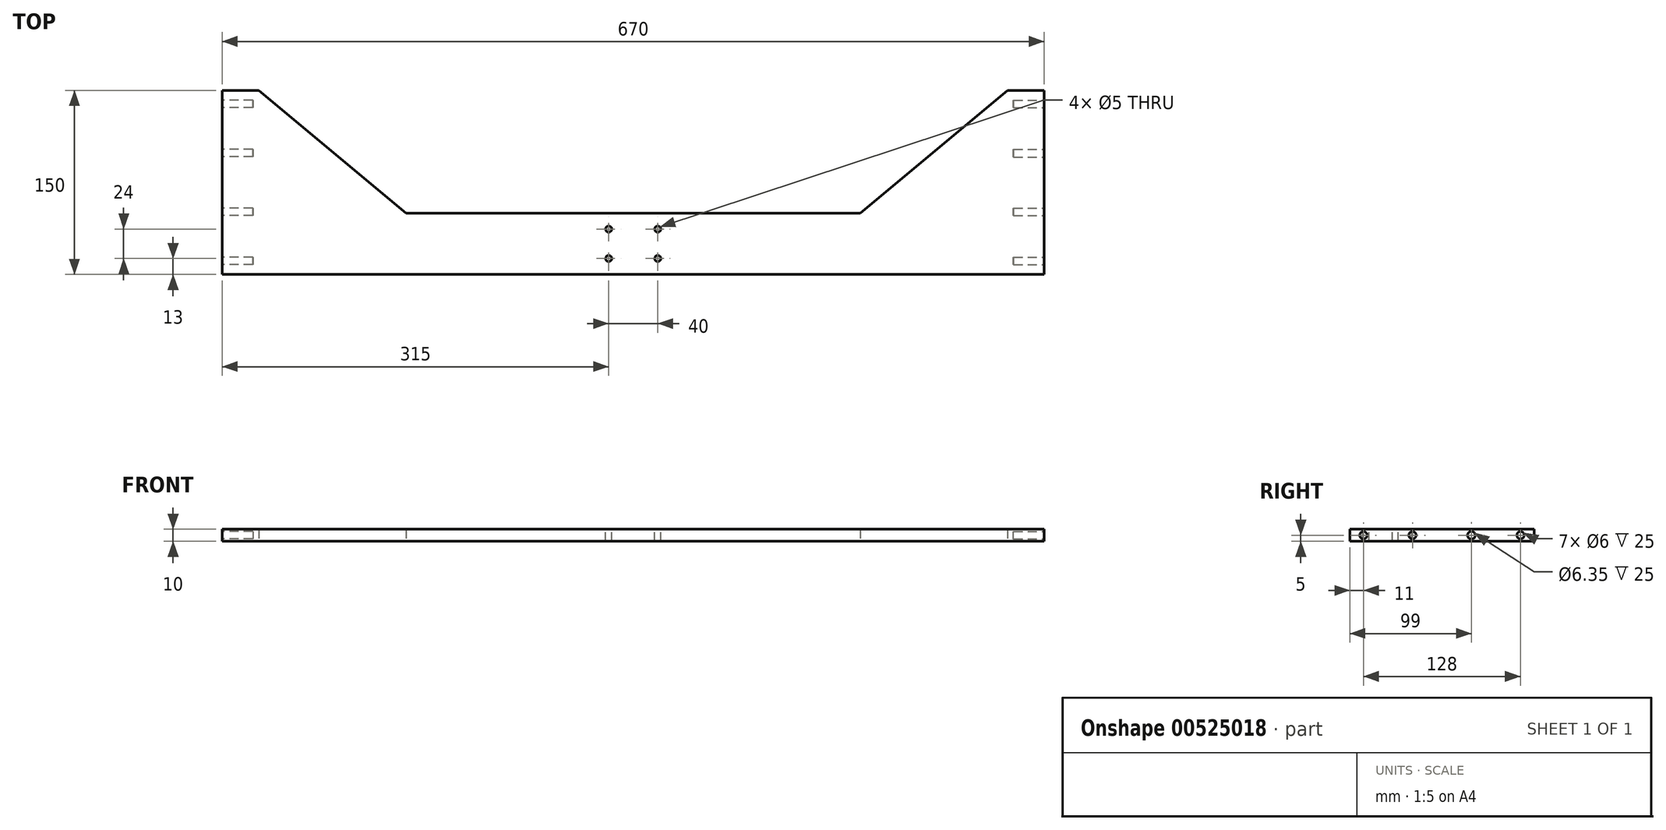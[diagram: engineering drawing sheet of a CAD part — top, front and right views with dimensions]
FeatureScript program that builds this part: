
annotation { "Feature Type Name" : "Feature", "Feature Type Description" : "" }
export const myFeature = defineFeature(function(context is Context, id is Id, definition is map)
    precondition{}
    {
        {
            var Q0;
            Q0=qCreatedBy(makeId("Top.planeOp"),FACE);
            var sketch = newSketch(context, id + "F0", { "sketchPlane" : qUnion([Q0])});
            skLineSegment(sketch, "E0.bottom", {"start": v(335, 25) * mm, "end": v(-335, 25) * mm});
            skLineSegment(sketch, "E0.top", {"start": v(335, -25) * mm, "end": v(-335, -25) * mm});
            skLineSegment(sketch, "E0.left", {"start": v(335, 25) * mm, "end": v(335, -25) * mm});
            skLineSegment(sketch, "E0.right", {"start": v(-335, 25) * mm, "end": v(-335, -25) * mm});
            skPoint(sketch, "E0.middle", {"position": v(0, 0) * mm});
            skLineSegment(sketch, "E1", {"start": v(335, 25) * mm, "end": v(335, 125) * mm});
            skLineSegment(sketch, "E2", {"start": v(335, 125) * mm, "end": v(305, 125) * mm});
            skLineSegment(sketch, "E3", {"start": v(305, 125) * mm, "end": v(185, 25) * mm});
            skLineSegment(sketch, "E4", {"start": v(-335, 25) * mm, "end": v(-335, 125) * mm});
            skLineSegment(sketch, "E5", {"start": v(-335, 125) * mm, "end": v(-305, 125) * mm});
            skLineSegment(sketch, "E6", {"start": v(-305, 125) * mm, "end": v(-185, 25) * mm});
            skSolve(sketch);
        }
        {
            var Q0;
            Q0 = qSketchRegion(id + "F0", true);
            extrude(context, id + "F1", {"entities" : qUnion([Q0]), "endBound" : BoundingType.SYMMETRIC, "depth" : 10 * mm, "offsetDistance" : 25 * mm});
        }
        {
            var Q0;
            Q0=makeQuery(id+"F1.opExtrude","SWEPT_FACE",FACE,{"disambiguationData":[OSD([sQuery(id+"F0.wireOp",EDGE,"E0.left")])]});
            var sketch = newSketch(context, id + "F2", { "sketchPlane" : qUnion([Q0])});
            skCircle(sketch, "E7", {"center": v(26, 0) * mm, "radius": 3 * mm});
            skCircle(sketch, "E8", {"center": v(-14, 0) * mm, "radius": 3 * mm});
            skCircle(sketch, "E9", {"center": v(74, 0) * mm, "radius": 3.18 * mm});
            skCircle(sketch, "E10", {"center": v(114, 0) * mm, "radius": 3 * mm});
            skSolve(sketch);
        }
        {
            var Q0;
            Q0 = qSketchRegion(id + "F2", true);
            extrude(context, id + "F3", {"entities" : qUnion([Q0]), "operationType" : NewBodyOperationType.REMOVE, "oppositeDirection" : true, "depth" : 25 * mm, "offsetDistance" : 25 * mm});
        }
        {
            var Q0;
            Q0=makeQuery(id+"F1.opExtrude","SWEPT_FACE",FACE,{"disambiguationData":[OSD([sQuery(id+"F0.wireOp",EDGE,"E0.right")])]});
            var sketch = newSketch(context, id + "F4", { "sketchPlane" : qUnion([Q0])});
            skCircle(sketch, "E11", {"center": v(14, 0) * mm, "radius": 3 * mm});
            skCircle(sketch, "E12", {"center": v(-26, 0) * mm, "radius": 3 * mm});
            skCircle(sketch, "E13", {"center": v(-74, 0) * mm, "radius": 3 * mm});
            skCircle(sketch, "E14", {"center": v(-114, 0) * mm, "radius": 3 * mm});
            skSolve(sketch);
        }
        {
            var Q0;
            Q0 = qSketchRegion(id + "F4", true);
            extrude(context, id + "F5", {"entities" : qUnion([Q0]), "operationType" : NewBodyOperationType.REMOVE, "oppositeDirection" : true, "depth" : 25 * mm, "offsetDistance" : 25 * mm});
        }
        {
            var Q0;
            Q0=makeQuery(id+"F1.opExtrude","CAP_FACE",FACE,{"disambiguationData":[OSD([sQuery(id+"F0.wireOp",EDGE,"E0.bottom"),sQuery(id+"F0.wireOp",EDGE,"E0.top"),sQuery(id+"F0.wireOp",EDGE,"E0.left"),sQuery(id+"F0.wireOp",EDGE,"E0.right")])],"isStart":false});
            var sketch = newSketch(context, id + "F6", { "sketchPlane" : qUnion([Q0])});
            skCircle(sketch, "E15", {"center": v(-20, 12) * mm, "radius": 2.5 * mm});
            skCircle(sketch, "E16", {"center": v(20, 12) * mm, "radius": 2.5 * mm});
            skCircle(sketch, "E17", {"center": v(20, -12) * mm, "radius": 2.5 * mm});
            skCircle(sketch, "E18", {"center": v(-20, -12) * mm, "radius": 2.5 * mm});
            skSolve(sketch);
        }
        {
            var Q0;
            Q0 = qSketchRegion(id + "F6", true);
            extrude(context, id + "F7", {"entities" : qUnion([Q0]), "operationType" : NewBodyOperationType.REMOVE, "oppositeDirection" : true, "depth" : 10 * mm, "offsetDistance" : 25 * mm});
        }
    });
